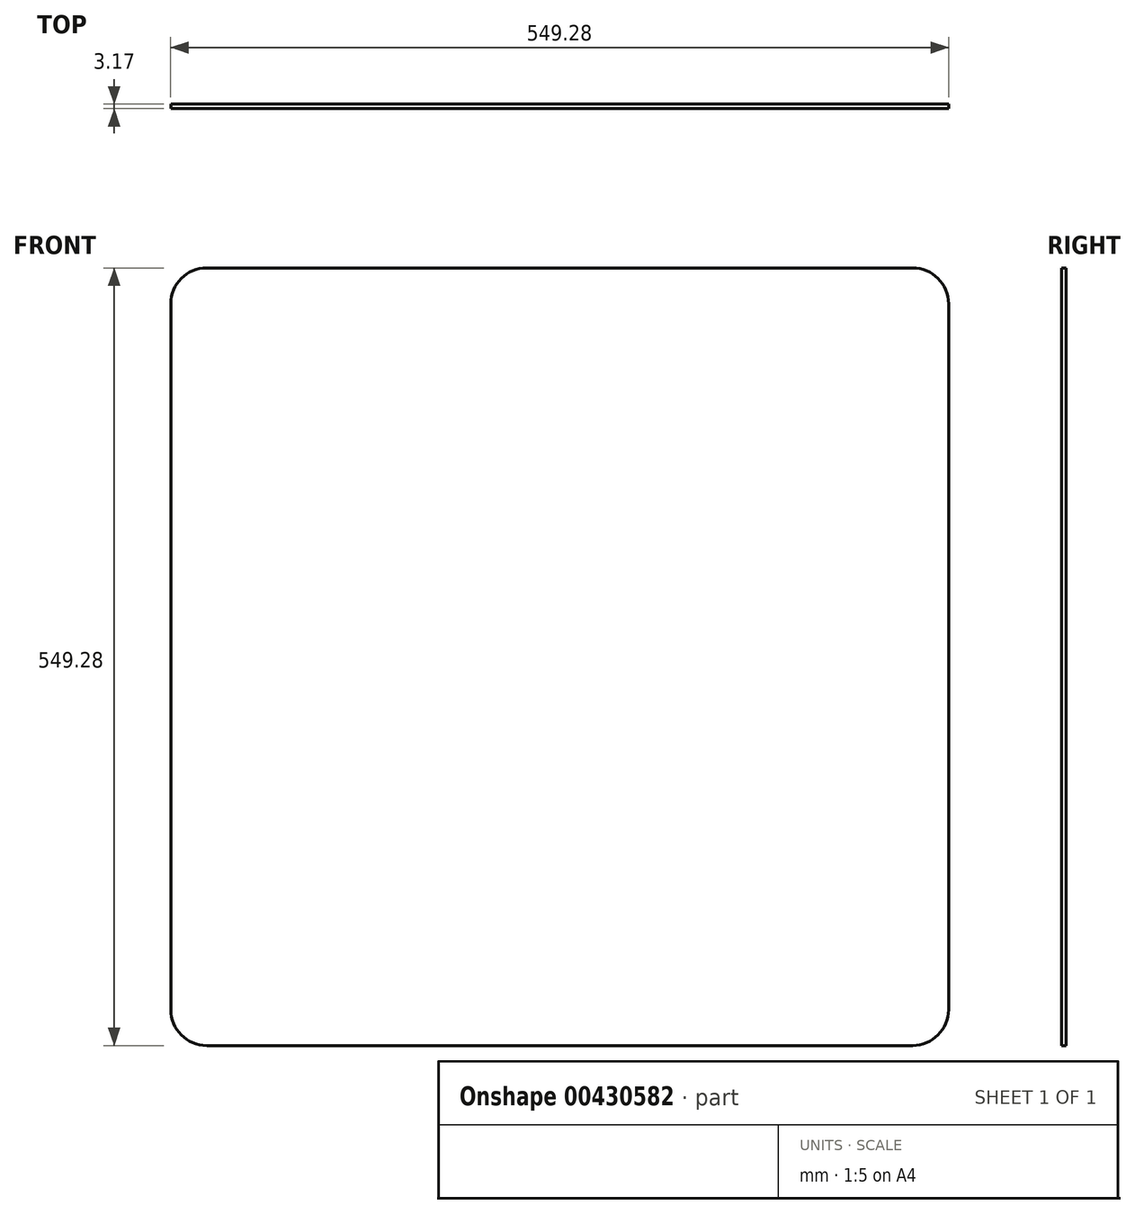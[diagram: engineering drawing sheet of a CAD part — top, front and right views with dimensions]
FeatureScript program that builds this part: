
annotation { "Feature Type Name" : "Feature", "Feature Type Description" : "" }
export const myFeature = defineFeature(function(context is Context, id is Id, definition is map)
    precondition{}
    {
        {
            var Q0;
            Q0=qCreatedBy(makeId("Front.planeOp"),FACE);
            var sketch = newSketch(context, id + "F0", { "sketchPlane" : qUnion([Q0])});
            skLineSegment(sketch, "E0.bottom", {"start": v(274.64, -274.64) * mm, "end": v(-274.64, -274.64) * mm});
            skLineSegment(sketch, "E0.top", {"start": v(274.64, 274.64) * mm, "end": v(-274.64, 274.64) * mm});
            skLineSegment(sketch, "E0.left", {"start": v(274.64, -274.64) * mm, "end": v(274.64, 274.64) * mm});
            skLineSegment(sketch, "E0.right", {"start": v(-274.64, -274.64) * mm, "end": v(-274.64, 274.64) * mm});
            skPoint(sketch, "E0.middle", {"position": v(0, 0) * mm});
            skSolve(sketch);
        }
        {
            var Q0;
            Q0=makeQuery(id+"F0.imprint","IMPRINT",FACE,{"disambiguationData":[TD([[makeQuery(id+"F0.imprint","IMPRINT",EDGE,{"derivedFrom":sQuery(id+"F0.wireOp",EDGE,"E0.bottom")}),-1.0]])]});
            extrude(context, id + "F1", {"entities" : qUnion([Q0]), "depth" : 3.17 * mm, "offsetDistance" : 25 * mm});
        }
        {
            var Q0;
            Q0=makeQuery(id+"F1.opExtrude","SWEPT_EDGE",EDGE,{"disambiguationData":[OSD([sQuery(id+"F0.wireOp",EDGE,"E0.bottom"),sQuery(id+"F0.wireOp",EDGE,"E0.right")])]});
            var Q1;
            Q1=makeQuery(id+"F1.opExtrude","SWEPT_EDGE",EDGE,{"disambiguationData":[OSD([sQuery(id+"F0.wireOp",EDGE,"E0.top"),sQuery(id+"F0.wireOp",EDGE,"E0.right")])]});
            var Q2;
            Q2=makeQuery(id+"F1.opExtrude","SWEPT_EDGE",EDGE,{"disambiguationData":[OSD([sQuery(id+"F0.wireOp",EDGE,"E0.top"),sQuery(id+"F0.wireOp",EDGE,"E0.left")])]});
            var Q3;
            Q3=makeQuery(id+"F1.opExtrude","SWEPT_EDGE",EDGE,{"disambiguationData":[OSD([sQuery(id+"F0.wireOp",EDGE,"E0.bottom"),sQuery(id+"F0.wireOp",EDGE,"E0.left")])]});
            fillet(context, id + "F2", {"entities" : qUnion([Q0, Q1, Q2, Q3]), "radius" : 25.4 * mm, "tangentPropagation" : true, "allowEdgeOverflow" : false});
        }
    });
